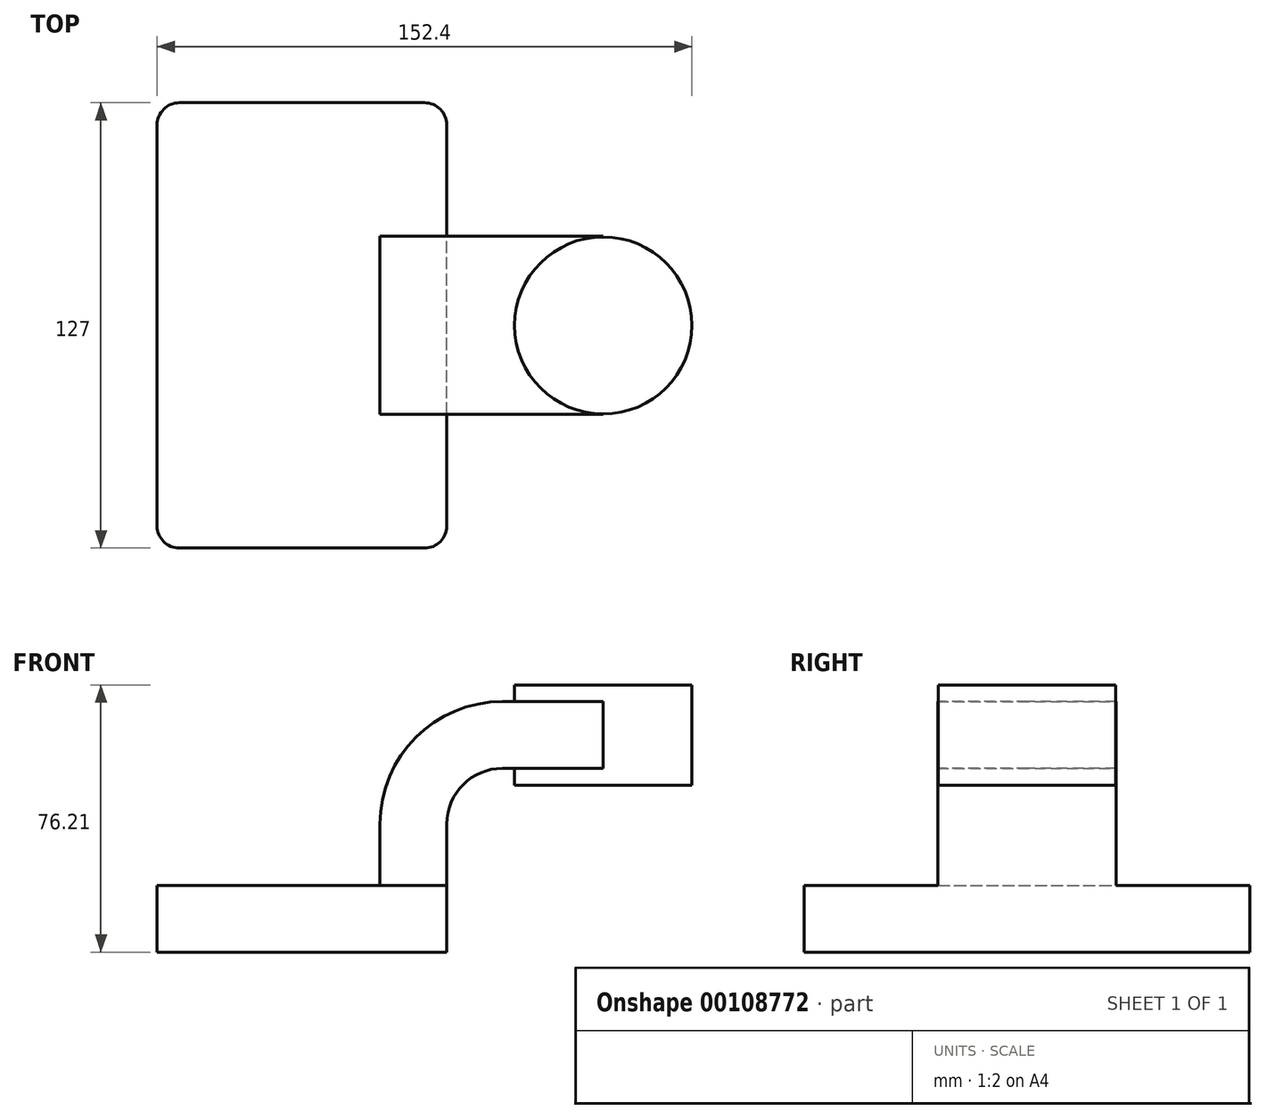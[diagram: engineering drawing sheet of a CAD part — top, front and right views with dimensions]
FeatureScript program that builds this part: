
annotation { "Feature Type Name" : "Feature", "Feature Type Description" : "" }
export const myFeature = defineFeature(function(context is Context, id is Id, definition is map)
    precondition{}
    {
        {
            var Q0;
            Q0=qCreatedBy(makeId("Front.planeOp"),FACE);
            var sketch = newSketch(context, id + "F0", { "sketchPlane" : qUnion([Q0])});
            skLineSegment(sketch, "E0.bottom", {"start": v(41.27, 9.53) * mm, "end": v(-41.28, 9.53) * mm});
            skLineSegment(sketch, "E0.top", {"start": v(41.28, -9.52) * mm, "end": v(-41.27, -9.52) * mm});
            skLineSegment(sketch, "E0.left", {"start": v(41.28, 9.53) * mm, "end": v(41.28, -9.52) * mm});
            skLineSegment(sketch, "E0.right", {"start": v(-41.28, 9.53) * mm, "end": v(-41.27, -9.52) * mm});
            skPoint(sketch, "E0.middle", {"position": v(0, 0) * mm});
            skLineSegment(sketch, "E1.bottom", {"start": v(60.33, 38.1) * mm, "end": v(111.12, 38.1) * mm});
            skLineSegment(sketch, "E1.top", {"start": v(60.33, 66.68) * mm, "end": v(111.12, 66.68) * mm});
            skLineSegment(sketch, "E1.left", {"start": v(60.33, 38.1) * mm, "end": v(60.33, 66.68) * mm});
            skLineSegment(sketch, "E1.right", {"start": v(111.12, 38.1) * mm, "end": v(111.12, 66.68) * mm});
            skPoint(sketch, "E1.middle", {"position": v(85.72, 52.39) * mm});
            skLineSegment(sketch, "E2", {"start": v(41.27, 9.53) * mm, "end": v(41.27, 27) * mm});
            skArc(sketch, "E3", {"start": v(41.27, 27) * mm, "mid": v(45.92, 38.23) * mm, "end": v(57.15, 42.88) * mm});
            skLineSegment(sketch, "E4", {"start": v(57.15, 42.88) * mm, "end": v(85.87, 42.88) * mm});
            skLineSegment(sketch, "E5.0", {"start": v(57.15, 61.93) * mm, "end": v(85.87, 61.93) * mm});
            skArc(sketch, "E5.1", {"start": v(22.23, 27) * mm, "mid": v(32.45, 51.7) * mm, "end": v(57.15, 61.93) * mm});
            skLineSegment(sketch, "E5.2", {"start": v(22.23, 9.53) * mm, "end": v(22.23, 27) * mm});
            skFitSpline(sketch, "E6", {"points": [v(-41.28, 9.53) * mm, v(57.15, 61.93) * mm], "startDerivative": vector(82.19, 74.17) * mm, "endDerivative": vector(143.1, -6.4) * mm});
            skLineSegment(sketch, "E7", {"start": v(85.87, 38.1) * mm, "end": v(85.87, 66.68) * mm});
            skSolve(sketch);
        }
        {
            var Q0;
            Q0=makeQuery(id+"F0.imprint","IMPRINT",FACE,{"disambiguationData":[TD([[makeQuery(id+"F0.imprint","IMPRINT",EDGE,{"derivedFrom":sQuery(id+"F0.wireOp",EDGE,"E0.top")}),-1.0]])]});
            extrude(context, id + "F1", {"entities" : qUnion([Q0]), "endBound" : BoundingType.SYMMETRIC, "depth" : 127 * mm});
        }
        {
            var Q0;
            {var subQ1=sQuery(id+"F0.wireOp",EDGE,"E2");Q0=makeQuery(id+"F0.imprint","IMPRINT",FACE,{"disambiguationData":[TD([[makeQuery(id+"F0.imprint","IMPRINT",EDGE,{"derivedFrom":subQ1}),1.0]])]});}
            var Q1;
            {var subQ0=sQuery(id+"F0.wireOp",EDGE,"E4");var subQ1=sQuery(id+"F0.wireOp",EDGE,"E1.left");var subQ2=makeQuery(id+"F0.imprint","INTERSECT",VERTEX,{"derivedFrom":[subQ1,subQ0]});Q1=makeQuery(id+"F0.imprint","IMPRINT",FACE,{"disambiguationData":[TD([[makeQuery(id+"F0.imprint","IMPRINT",EDGE,{"disambiguationData":[TD([[subQ2,-1.0]])],"derivedFrom":subQ1}),-1.0]])]});}
            extrude(context, id + "F2", {"entities" : qUnion([Q0, Q1]), "operationType" : NewBodyOperationType.ADD, "endBound" : BoundingType.SYMMETRIC, "depth" : 50.8 * mm});
        }
        {
            var Q0;
            Q0=makeQuery(id+"F0.imprint","IMPRINT",FACE,{"disambiguationData":[TD([[makeQuery(id+"F0.imprint","IMPRINT",EDGE,{"derivedFrom":sQuery(id+"F0.wireOp",EDGE,"E5.1")}),1.0]])]});
            extrude(context, id + "F3", {"entities" : qUnion([Q0]), "operationType" : NewBodyOperationType.ADD, "endBound" : BoundingType.SYMMETRIC, "depth" : 15.88 * mm});
        }
        {
            var Q0;
            {var subQ0=sQuery(id+"F0.wireOp",EDGE,"E1.right");Q0=makeQuery(id+"F0.imprint","IMPRINT",FACE,{"disambiguationData":[TD([[makeQuery(id+"F0.imprint","IMPRINT",EDGE,{"derivedFrom":subQ0}),1.0]])]});}
            var Q1;
            Q1=sQuery(id+"F0.wireOp",EDGE,"E7");
            revolve(context, id + "F4", {"operationType" : NewBodyOperationType.ADD, "entities" : qUnion([Q0]), "axis" : qUnion([Q1]), "revolveType" : RevolveType.FULL});
        }
        {
            var Q0;
            Q0=makeQuery(id+"F1.opExtrude","CAP_EDGE",EDGE,{"disambiguationData":[OSD([sQuery(id+"F0.wireOp",EDGE,"E0.right")])],"isStart":false});
            var Q1;
            Q1=makeQuery(id+"F1.opExtrude","CAP_EDGE",EDGE,{"disambiguationData":[OSD([sQuery(id+"F0.wireOp",EDGE,"E0.left")])],"isStart":false});
            var Q2;
            Q2=makeQuery(id+"F1.opExtrude","CAP_EDGE",EDGE,{"disambiguationData":[OSD([sQuery(id+"F0.wireOp",EDGE,"E0.left")])],"isStart":true});
            var Q3;
            Q3=makeQuery(id+"F1.opExtrude","CAP_EDGE",EDGE,{"disambiguationData":[OSD([sQuery(id+"F0.wireOp",EDGE,"E0.right")])],"isStart":true});
            fillet(context, id + "F5", {"entities" : qUnion([Q0, Q1, Q2, Q3]), "radius" : 6.35 * mm, "tangentPropagation" : true, "allowEdgeOverflow" : false});
        }
    });
